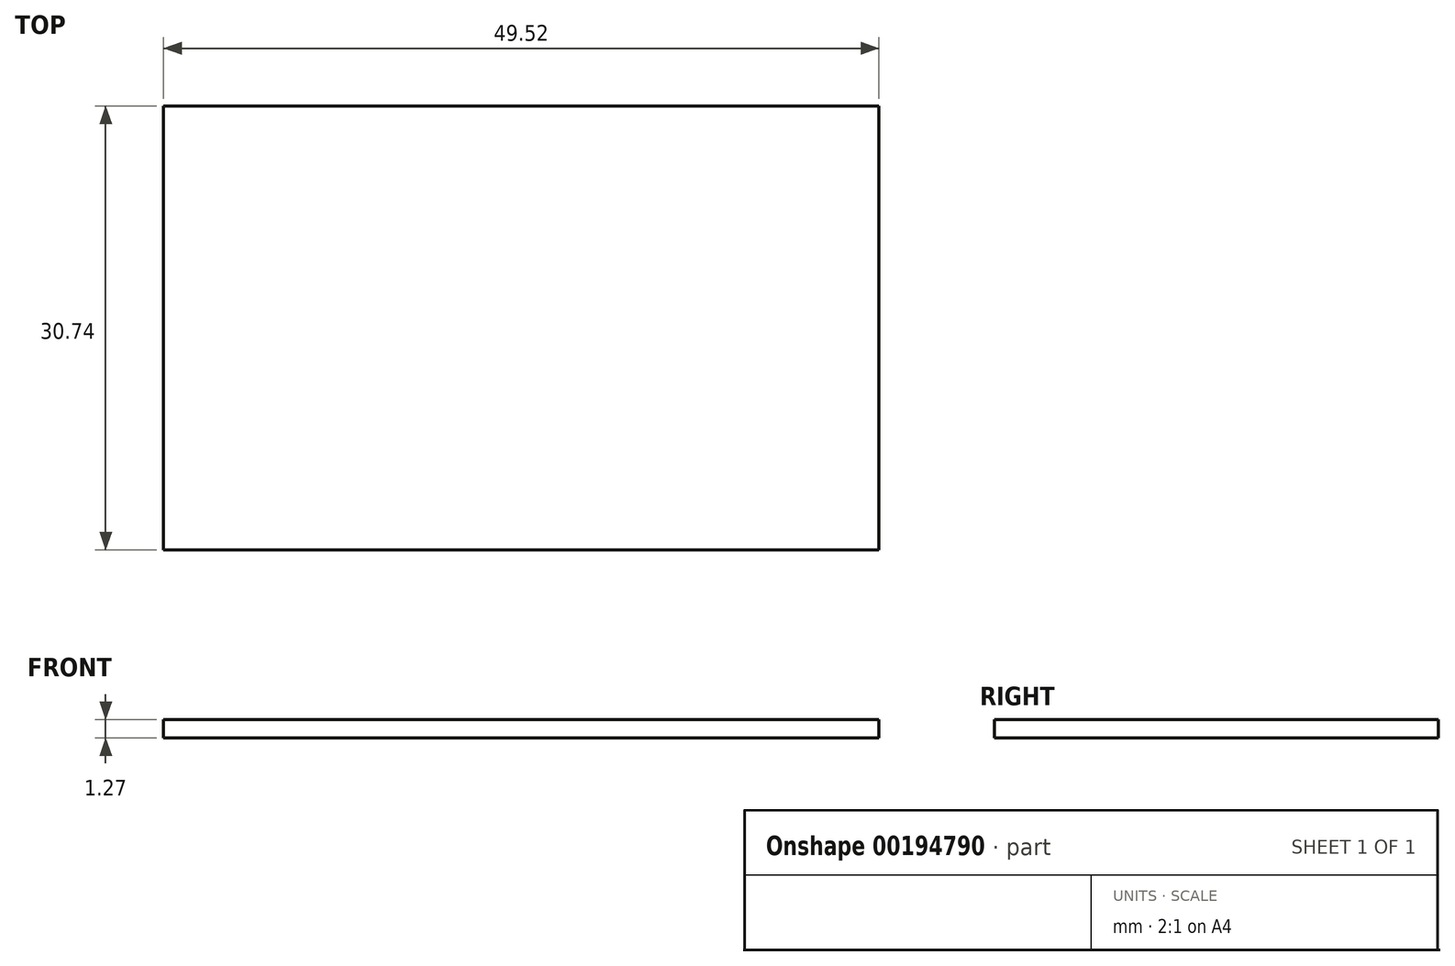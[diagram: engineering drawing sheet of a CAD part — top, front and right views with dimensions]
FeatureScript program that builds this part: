
annotation { "Feature Type Name" : "Feature", "Feature Type Description" : "" }
export const myFeature = defineFeature(function(context is Context, id is Id, definition is map)
    precondition{}
    {
        {
            var Q0;
            Q0=qCreatedBy(makeId("Top.planeOp"),FACE);
            var sketch = newSketch(context, id + "F0", { "sketchPlane" : qUnion([Q0])});
            skLineSegment(sketch, "E0.bottom", {"start": v(0, 0) * mm, "end": v(-49.52, 0) * mm});
            skLineSegment(sketch, "E0.top", {"start": v(0, 30.74) * mm, "end": v(-49.52, 30.74) * mm});
            skLineSegment(sketch, "E0.left", {"start": v(0, 0) * mm, "end": v(0, 30.74) * mm});
            skLineSegment(sketch, "E0.right", {"start": v(-49.52, 0) * mm, "end": v(-49.52, 30.74) * mm});
            skSolve(sketch);
        }
        {
            var Q0;
            Q0=makeQuery(id+"F0.imprint","IMPRINT",FACE,{"disambiguationData":[TD([[makeQuery(id+"F0.imprint","IMPRINT",EDGE,{"derivedFrom":sQuery(id+"F0.wireOp",EDGE,"E0.bottom")}),-1.0]])]});
            extrude(context, id + "F1", {"entities" : qUnion([Q0]), "depth" : 1.27 * mm});
        }
    });
